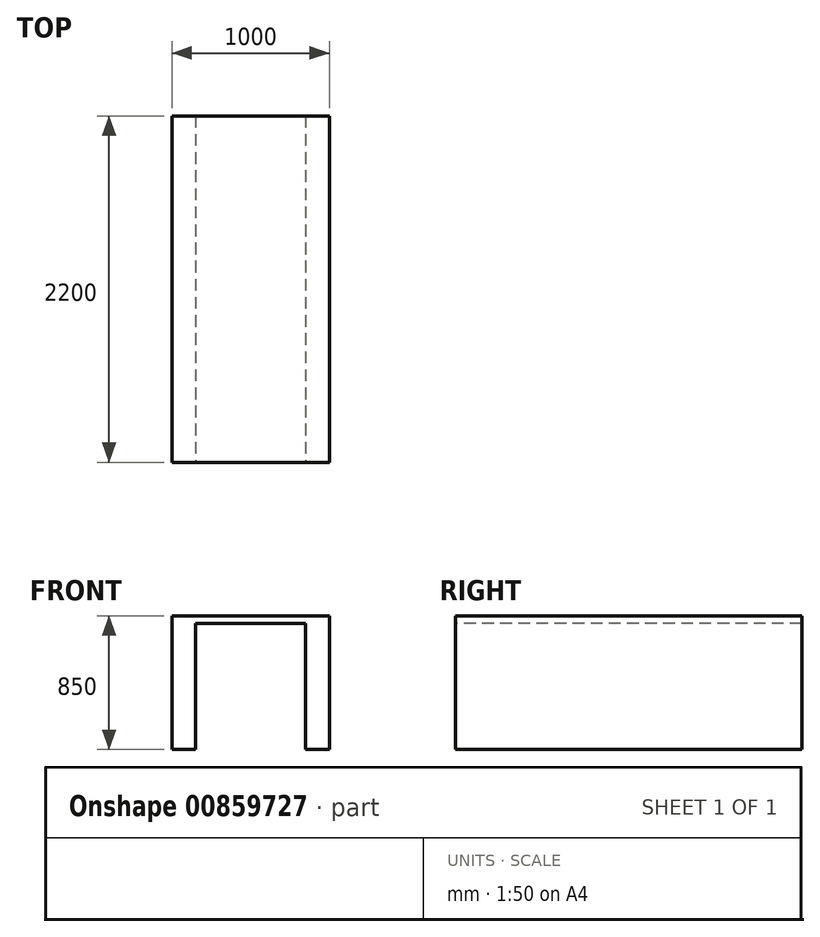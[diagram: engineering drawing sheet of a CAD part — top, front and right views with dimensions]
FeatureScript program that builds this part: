
annotation { "Feature Type Name" : "Feature", "Feature Type Description" : "" }
export const myFeature = defineFeature(function(context is Context, id is Id, definition is map)
    precondition{}
    {
        {
            var Q0;
            Q0=qCreatedBy(makeId("Front.planeOp"),FACE);
            var sketch = newSketch(context, id + "F0", { "sketchPlane" : qUnion([Q0])});
            skLineSegment(sketch, "E0.bottom", {"start": v(-504.12, 850) * mm, "end": v(495.88, 850) * mm});
            skLineSegment(sketch, "E0.top", {"start": v(-504.12, 800) * mm, "end": v(495.88, 800) * mm});
            skLineSegment(sketch, "E0.left", {"start": v(-504.12, 850) * mm, "end": v(-504.12, 800) * mm});
            skLineSegment(sketch, "E0.right", {"start": v(495.88, 850) * mm, "end": v(495.88, 800) * mm});
            skSolve(sketch);
        }
        {
            var Q0;
            Q0 = qSketchRegion(id + "F0", true);
            extrude(context, id + "F1", {"entities" : qUnion([Q0]), "depth" : 2200 * mm, "offsetDistance" : 25 * mm});
        }
        {
            var Q0;
            Q0=makeQuery(id+"F1.opExtrude","CAP_FACE",FACE,{"disambiguationData":[OSD([sQuery(id+"F0.wireOp",EDGE,"E0.bottom"),sQuery(id+"F0.wireOp",EDGE,"E0.top"),sQuery(id+"F0.wireOp",EDGE,"E0.left"),sQuery(id+"F0.wireOp",EDGE,"E0.right")])],"isStart":false});
            var sketch = newSketch(context, id + "F2", { "sketchPlane" : qUnion([Q0])});
            skLineSegment(sketch, "E1.bottom", {"start": v(495.88, 800) * mm, "end": v(345.88, 800) * mm});
            skLineSegment(sketch, "E1.top", {"start": v(495.88, 0) * mm, "end": v(345.88, 0) * mm});
            skLineSegment(sketch, "E1.left", {"start": v(495.88, 800) * mm, "end": v(495.88, 0) * mm});
            skLineSegment(sketch, "E1.right", {"start": v(345.88, 800) * mm, "end": v(345.88, 0) * mm});
            skLineSegment(sketch, "E2.bottom", {"start": v(-504.12, 800) * mm, "end": v(-354.12, 800) * mm});
            skLineSegment(sketch, "E2.top", {"start": v(-504.12, 0) * mm, "end": v(-354.12, 0) * mm});
            skLineSegment(sketch, "E2.left", {"start": v(-504.12, 800) * mm, "end": v(-504.12, 0) * mm});
            skLineSegment(sketch, "E2.right", {"start": v(-354.12, 800) * mm, "end": v(-354.12, 0) * mm});
            skSolve(sketch);
        }
        {
            var Q0;
            Q0 = qSketchRegion(id + "F2", true);
            var Q1;
            Q1=makeQuery(id+"F1.opExtrude","CAP_FACE",FACE,{"disambiguationData":[OSD([sQuery(id+"F0.wireOp",EDGE,"E0.bottom"),sQuery(id+"F0.wireOp",EDGE,"E0.top"),sQuery(id+"F0.wireOp",EDGE,"E0.left"),sQuery(id+"F0.wireOp",EDGE,"E0.right")])],"isStart":true});
            extrude(context, id + "F3", {"entities" : qUnion([Q0]), "operationType" : NewBodyOperationType.ADD, "endBound" : BoundingType.UP_TO_SURFACE, "oppositeDirection" : true, "depth" : 25 * mm, "endBoundEntityFace" : qUnion([Q1]), "offsetDistance" : 25 * mm});
        }
    });
